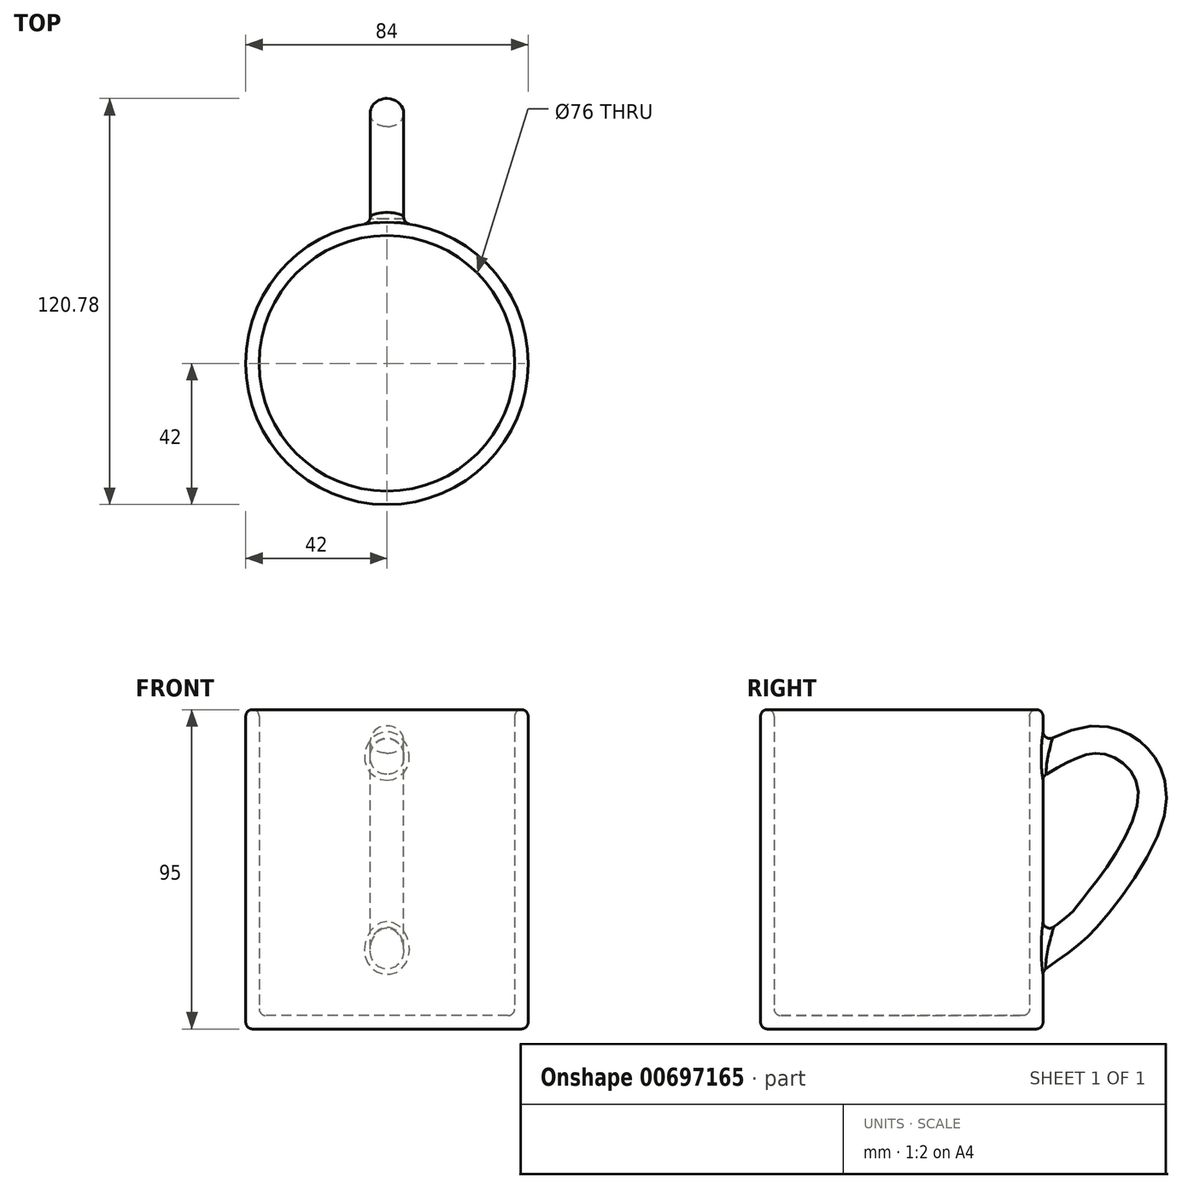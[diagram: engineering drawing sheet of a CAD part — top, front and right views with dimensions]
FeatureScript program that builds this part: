
annotation { "Feature Type Name" : "Feature", "Feature Type Description" : "" }
export const myFeature = defineFeature(function(context is Context, id is Id, definition is map)
    precondition{}
    {
        {
            var Q0;
            Q0=qCreatedBy(makeId("Top.planeOp"),FACE);
            var sketch = newSketch(context, id + "F0", { "sketchPlane" : qUnion([Q0])});
            skCircle(sketch, "E0", {"center": v(0, 0) * mm, "radius": 42 * mm});
            skSolve(sketch);
        }
        {
            var Q0;
            Q0=makeQuery(id+"F0.imprint","IMPRINT",FACE,{"disambiguationData":[TD([[makeQuery(id+"F0.imprint","IMPRINT",EDGE,{"derivedFrom":sQuery(id+"F0.wireOp",EDGE,"E0")}),1.0]])]});
            extrude(context, id + "F1", {"entities" : qUnion([Q0]), "depth" : 95 * mm, "offsetDistance" : 25 * mm});
        }
        {
            var Q0;
            Q0=qCreatedBy(makeId("Right.planeOp"),FACE);
            var sketch = newSketch(context, id + "F2", { "sketchPlane" : qUnion([Q0])});
            skFitSpline(sketch, "E1", {"points": [v(37.86, 77.4) * mm, v(60.17, 85.27) * mm, v(74.02, 69.32) * mm, v(55.49, 34.6) * mm, v(37.2, 19.57) * mm], "startDerivative": vector(93.9, 52.55) * mm, "endDerivative": vector(-167.9, -123.66) * mm});
            skSolve(sketch);
        }
        {
            var Q0;
            Q0=qCreatedBy(makeId("Front.planeOp"),FACE);
            cPlane(context, id + "F3", {"entities" : qUnion([Q0]), "cplaneType" : CPlaneType.OFFSET, "offset" : 36.6 * mm, "oppositeDirection" : true, "width" : 150 * mm, "height" : 150 * mm});
        }
        {
            var Q0;
            Q0=qCreatedBy(id+"F3.planeOp",FACE);
            var sketch = newSketch(context, id + "F4", { "sketchPlane" : qUnion([Q0])});
            skCircle(sketch, "E2", {"center": v(0, 77.1) * mm, "radius": 5 * mm});
            skSolve(sketch);
        }
        {
            var Q0;
            Q0 = qSketchRegion(id + "F4", true);
            var Q1;
            Q1 = qConstructionFilter(qBodyType(qCreatedBy(id + "F2" ,EDGE), BodyType.WIRE), ConstructionObject.NO);
            sweep(context, id + "F5", {"operationType" : NewBodyOperationType.ADD, "profiles" : qUnion([Q0]), "path" : qUnion([Q1])});
        }
        {
            var Q0;
            Q0=makeQuery(id+"F1.opExtrude","CAP_FACE",FACE,{"disambiguationData":[OSD([sQuery(id+"F0.wireOp",EDGE,"E0")])],"isStart":false});
            shell(context, id + "F6", {"entities" : qUnion([Q0]), "thickness" : 4 * mm});
        }
        {
            var Q0;
            {var subQ0=sQuery(id+"F0.wireOp",EDGE,"E0");Q0=makeQuery(id+"F6.opShell","OFFSET_FACE",FACE,{"disambiguationData":[OSD([subQ0]),TDD([makeQuery(id+"F1.opExtrude","SWEPT_FACE",FACE,{"disambiguationData":[OSD([subQ0])]})])]});}
            var Q1;
            Q1=makeQuery(id+"F1.opExtrude","CAP_EDGE",EDGE,{"disambiguationData":[OSD([sQuery(id+"F0.wireOp",EDGE,"E0")])],"isStart":false});
            var Q2;
            Q2=makeQuery(id+"F5.boolean.opBoolean","INTERSECT",EDGE,{"disambiguationData":[OD(0.0)],"derivedFrom":[makeQuery(id+"F1.opExtrude","SWEPT_FACE",FACE,{"disambiguationData":[OSD([sQuery(id+"F0.wireOp",EDGE,"E0")])]}),makeQuery(id+"F5.opSweep","SWEPT_FACE",FACE,{"disambiguationData":[OSD([sQuery(id+"F2.wireOp",EDGE,"E1"),sQuery(id+"F4.wireOp",EDGE,"E2")])]})]});
            var Q3;
            Q3=makeQuery(id+"F5.boolean.opBoolean","INTERSECT",EDGE,{"disambiguationData":[OD(1.0)],"derivedFrom":[makeQuery(id+"F1.opExtrude","SWEPT_FACE",FACE,{"disambiguationData":[OSD([sQuery(id+"F0.wireOp",EDGE,"E0")])]}),makeQuery(id+"F5.opSweep","SWEPT_FACE",FACE,{"disambiguationData":[OSD([sQuery(id+"F2.wireOp",EDGE,"E1"),sQuery(id+"F4.wireOp",EDGE,"E2")])]})]});
            var Q4;
            Q4=makeQuery(id+"F1.opExtrude","SWEPT_FACE",FACE,{"disambiguationData":[OSD([sQuery(id+"F0.wireOp",EDGE,"E0")])]});
            var Q5;
            {var subQ0=sQuery(id+"F0.wireOp",EDGE,"E0");Q5=makeQuery(id+"F6.opShell","OFFSET_EDGE",EDGE,{"disambiguationData":[OSD([subQ0]),TDD([makeQuery(id+"F1.opExtrude","CAP_EDGE",EDGE,{"disambiguationData":[OSD([subQ0])],"isStart":true})])]});}
            var Q6;
            Q6=makeQuery(id+"F1.opExtrude","CAP_EDGE",EDGE,{"disambiguationData":[OSD([sQuery(id+"F0.wireOp",EDGE,"E0")])],"isStart":true});
            fillet(context, id + "F7", {"entities" : qUnion([Q0, Q1, Q2, Q3, Q4, Q5, Q6]), "radius" : 2 * mm, "tangentPropagation" : true, "allowEdgeOverflow" : false});
        }
    });
